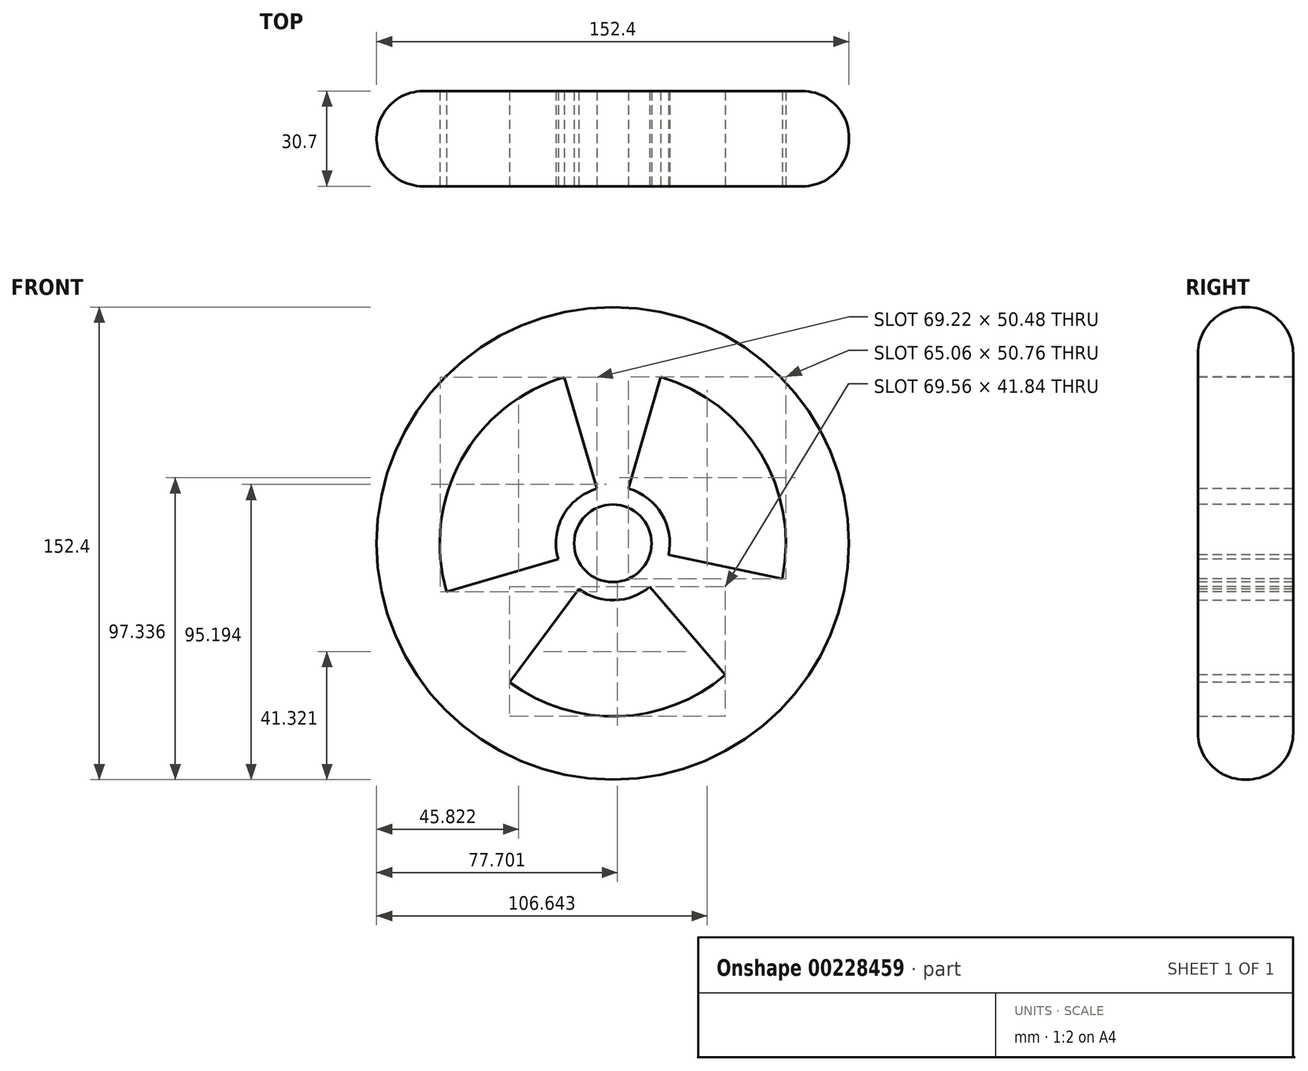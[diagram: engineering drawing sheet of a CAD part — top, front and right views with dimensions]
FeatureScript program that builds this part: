
annotation { "Feature Type Name" : "Feature", "Feature Type Description" : "" }
export const myFeature = defineFeature(function(context is Context, id is Id, definition is map)
    precondition{}
    {
        {
            var Q0;
            Q0=qCreatedBy(makeId("Front.planeOp"),FACE);
            var sketch = newSketch(context, id + "F0", { "sketchPlane" : qUnion([Q0])});
            skCircle(sketch, "E0", {"center": v(0, 0) * mm, "radius": 76.2 * mm});
            skSolve(sketch);
        }
        {
            var Q0;
            Q0 = qSketchRegion(id + "F0", true);
            extrude(context, id + "F1", {"entities" : qUnion([Q0]), "depth" : 30.7 * mm});
        }
        {
            var Q0;
            Q0=makeQuery(id+"F1.opExtrude","CAP_FACE",FACE,{"disambiguationData":[OSD([sQuery(id+"F0.wireOp",EDGE,"E0")])],"isStart":false});
            var sketch = newSketch(context, id + "F2", { "sketchPlane" : qUnion([Q0])});
            skCircle(sketch, "E1", {"center": v(0, 0) * mm, "radius": 11.9 * mm});
            skSolve(sketch);
        }
        {
            var Q0;
            Q0=sQuery(id+"F2.wireOp",VERTEX,"E1.center");
            var Q1;
            Q1=makeQuery(id+"F1.opExtrude","SWEPT_BODY",BODY,{"disambiguationData":[OSD([sQuery(id+"F0.wireOp",EDGE,"E0")])]});
            hole(context, id + "F3", {"style" : HoleStyle.SIMPLE, "endStyle" : HoleEndStyle.THROUGH, "holeDiameter" : 25 * mm, "locations" : qUnion([Q0]), "scope" : qUnion([Q1]), "isTappedThrough" : true});
        }
        {
            var Q0;
            Q0=makeQuery(id+"F1.opExtrude","CAP_FACE",FACE,{"disambiguationData":[OSD([sQuery(id+"F0.wireOp",EDGE,"E0")])],"isStart":false});
            var sketch = newSketch(context, id + "F4", { "sketchPlane" : qUnion([Q0])});
            skSolve(sketch);
        }
        {
            var Q0;
            Q0=makeQuery(id+"F4.imprint","IMPRINT",FACE,{"disambiguationData":[TD([[makeQuery(id+"F4.imprint","IMPRINT",EDGE,{"derivedFrom":makeQuery(id+"F1.opExtrude","CAP_EDGE",EDGE,{"disambiguationData":[OSD([sQuery(id+"F0.wireOp",EDGE,"E0")])],"isStart":false})}),1.0]])]});
            var sketch = newSketch(context, id + "F5", { "sketchPlane" : qUnion([Q0])});
            skLineSegment(sketch, "E2", {"start": v(0, 0) * mm, "end": v(0, 55.83) * mm});
            skCircle(sketch, "E3", {"center": v(0, 0) * mm, "radius": 55.83 * mm});
            skCircle(sketch, "E4", {"center": v(0, 0) * mm, "radius": 18.36 * mm});
            skLineSegment(sketch, "E5", {"start": v(0, 0) * mm, "end": v(-15.61, 53.6) * mm});
            skLineSegment(sketch, "E6", {"start": v(0, 0) * mm, "end": v(15.4, 53.67) * mm});
            skLineSegment(sketch, "E7", {"start": v(0, 0) * mm, "end": v(54.66, -11.4) * mm});
            skLineSegment(sketch, "E8", {"start": v(0, 0) * mm, "end": v(36.28, -42.44) * mm});
            skLineSegment(sketch, "E9", {"start": v(0, 0) * mm, "end": v(-53.6, -15.61) * mm});
            skLineSegment(sketch, "E10", {"start": v(0, 0) * mm, "end": v(-33.28, -44.83) * mm});
            skSolve(sketch);
        }
        {
            var Q0;
            {var subQ0=sQuery(id+"F5.wireOp",EDGE,"E5");var subQ1=sQuery(id+"F5.wireOp",EDGE,"E3");var subQ2=makeQuery(id+"F5.imprint","INTERSECT",VERTEX,{"derivedFrom":[subQ1,subQ0]});Q0=makeQuery(id+"F5.imprint","IMPRINT",FACE,{"disambiguationData":[TD([[makeQuery(id+"F5.imprint","IMPRINT",EDGE,{"disambiguationData":[TD([[subQ2,-1.0]])],"derivedFrom":subQ1}),1.0]])]});}
            var Q1;
            {var subQ0=sQuery(id+"F5.wireOp",EDGE,"E6");var subQ1=sQuery(id+"F5.wireOp",EDGE,"E3");var subQ2=makeQuery(id+"F5.imprint","INTERSECT",VERTEX,{"derivedFrom":[subQ1,subQ0]});Q1=makeQuery(id+"F5.imprint","IMPRINT",FACE,{"disambiguationData":[TD([[makeQuery(id+"F5.imprint","IMPRINT",EDGE,{"disambiguationData":[TD([[subQ2,1.0]])],"derivedFrom":subQ1}),1.0]])]});}
            var Q2;
            {var subQ0=sQuery(id+"F5.wireOp",EDGE,"E8");var subQ1=sQuery(id+"F5.wireOp",EDGE,"E3");var subQ2=makeQuery(id+"F5.imprint","INTERSECT",VERTEX,{"derivedFrom":[subQ1,subQ0]});Q2=makeQuery(id+"F5.imprint","IMPRINT",FACE,{"disambiguationData":[TD([[makeQuery(id+"F5.imprint","IMPRINT",EDGE,{"disambiguationData":[TD([[subQ2,1.0]])],"derivedFrom":subQ1}),1.0]])]});}
            extrude(context, id + "F6", {"entities" : qUnion([Q0, Q1, Q2]), "operationType" : NewBodyOperationType.REMOVE, "oppositeDirection" : true, "depth" : 50 * mm});
        }
        {
            var Q0;
            Q0=makeQuery(id+"F1.opExtrude","CAP_EDGE",EDGE,{"disambiguationData":[OSD([sQuery(id+"F0.wireOp",EDGE,"E0")])],"isStart":false});
            var Q1;
            Q1=makeQuery(id+"F1.opExtrude","SWEPT_FACE",FACE,{"disambiguationData":[OSD([sQuery(id+"F0.wireOp",EDGE,"E0")])]});
            fillet(context, id + "F7", {"entities" : qUnion([Q0, Q1]), "radius" : 15 * mm, "tangentPropagation" : true, "allowEdgeOverflow" : false});
        }
    });
